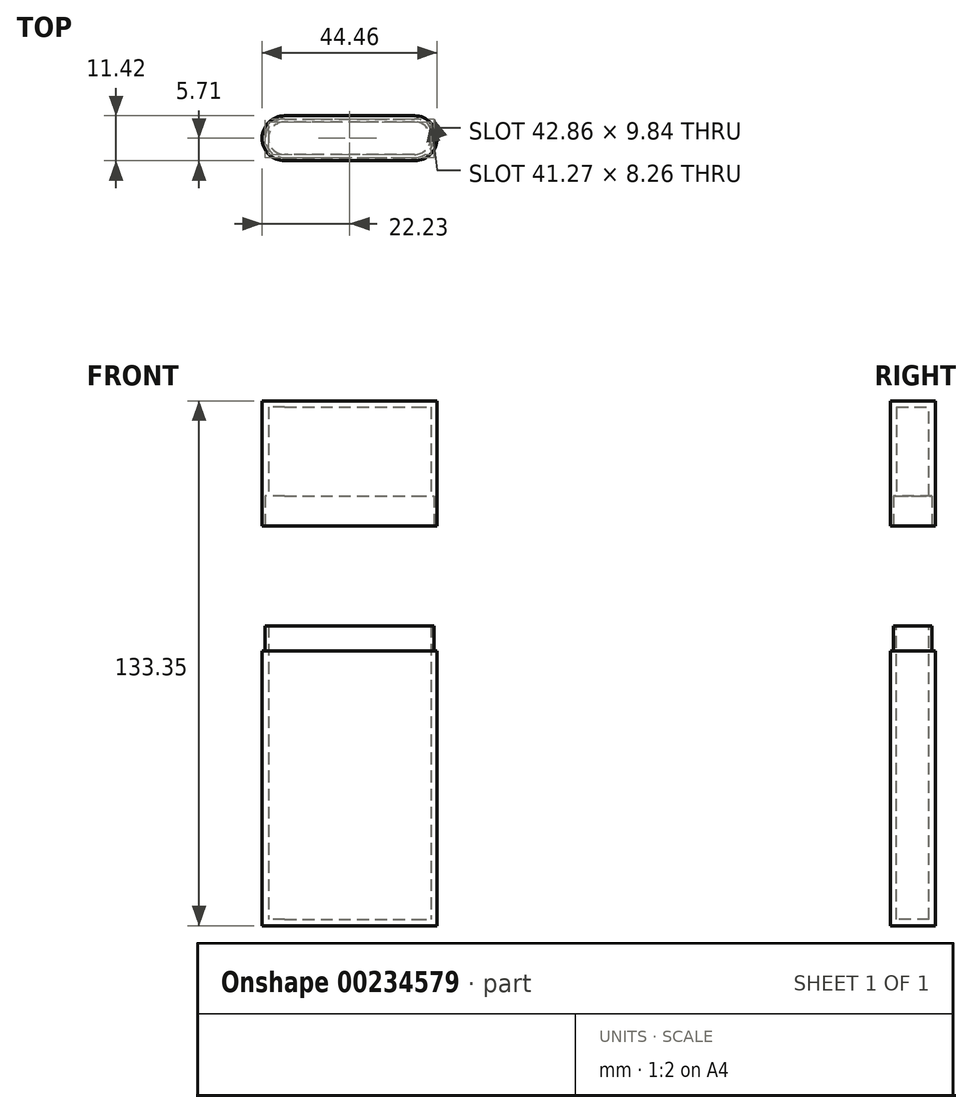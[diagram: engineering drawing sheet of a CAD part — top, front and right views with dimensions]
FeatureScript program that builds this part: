
annotation { "Feature Type Name" : "Feature", "Feature Type Description" : "" }
export const myFeature = defineFeature(function(context is Context, id is Id, definition is map)
    precondition{}
    {
        {
            var Q0;
            Q0=qCreatedBy(makeId("Top.planeOp"),FACE);
            var sketch = newSketch(context, id + "F0", { "sketchPlane" : qUnion([Q0])});
            skLineSegment(sketch, "E0.0", {"start": v(-16.51, 5.72) * mm, "end": v(16.51, 5.72) * mm});
            skArc(sketch, "E0.1", {"start": v(-16.51, 5.72) * mm, "mid": v(-22.23, 0) * mm, "end": v(-16.51, -5.72) * mm});
            skLineSegment(sketch, "E0.2", {"start": v(-16.51, -5.72) * mm, "end": v(16.51, -5.72) * mm});
            skArc(sketch, "E0.3", {"start": v(16.51, -5.72) * mm, "mid": v(22.23, 0) * mm, "end": v(16.51, 5.72) * mm});
            skPoint(sketch, "E1.start.orphan", {"position": v(-16.51, 4.13) * mm});
            skPoint(sketch, "E2.start.orphan", {"position": v(-16.51, -4.13) * mm});
            skSolve(sketch);
        }
        {
            assignVariable(context, id + "F1", {"mode" : VariableMode.ASSIGNED, "variableType" : VariableType.LENGTH, "measurementMode" : VariableMeasurementMode.DISTANCE, "name" : "Long", "lengthValue" : 76.2 * mm, "minmax" : VariableMinMaxSelection.MINIMUM, "extendEntities" : false, "measureFromAxis" : false, "distance" : 0 * mm, "xOffset" : 0 * mm, "yOffset" : 0 * mm, "zOffset" : 0 * mm, "componentSelector" : AxisWithCustom.DISTANCE, "customOffset" : 0 * mm, "radius" : false, "description" : ""});
        }
        {
            var Q0;
            Q0 = qSketchRegion(id + "F0", true);
            extrude(context, id + "F2", {"entities" : qUnion([Q0]), "flatOperationType" : FlatOperationType.REMOVE, "thickness1" : 6.35 * mm, "thickness2" : 0 * mm, "thickness" : 6.35 * mm, "offsetDistance" : 25.4 * mm, "startOffsetBound" : StartOffsetType.BLIND, "startOffsetDistance" : 25.4 * mm, "depth" : getVariable(context, 'Long'), "domain" : OperationDomain.MODEL});
        }
        {
            var Q0;
            Q0=makeQuery(id+"F2.opExtrude","CAP_FACE",FACE,{"disambiguationData":[OSD([sQuery(id+"F0.wireOp",EDGE,"E0.0"),sQuery(id+"F0.wireOp",EDGE,"E0.1"),sQuery(id+"F0.wireOp",EDGE,"E0.2"),sQuery(id+"F0.wireOp",EDGE,"E0.3")])],"isStart":false});
            shell(context, id + "F3", {"entities" : qUnion([Q0]), "thickness" : 1.59 * mm});
        }
        {
            var Q0;
            Q0=makeQuery(id+"F2.opExtrude","CAP_FACE",FACE,{"disambiguationData":[OSD([sQuery(id+"F0.wireOp",EDGE,"E0.0"),sQuery(id+"F0.wireOp",EDGE,"E0.1"),sQuery(id+"F0.wireOp",EDGE,"E0.2"),sQuery(id+"F0.wireOp",EDGE,"E0.3")])],"isStart":false});
            var sketch = newSketch(context, id + "F4", { "sketchPlane" : qUnion([Q0])});
            skArc(sketch, "E3.0", {"start": v(-16.51, 4.92) * mm, "mid": v(-21.43, 0) * mm, "end": v(-16.51, -4.92) * mm});
            skLineSegment(sketch, "E3.1", {"start": v(-16.51, 4.92) * mm, "end": v(16.51, 4.92) * mm});
            skArc(sketch, "E3.2", {"start": v(16.51, -4.92) * mm, "mid": v(21.43, 0) * mm, "end": v(16.51, 4.92) * mm});
            skLineSegment(sketch, "E3.3", {"start": v(-16.51, -4.92) * mm, "end": v(16.51, -4.92) * mm});
            skLineSegment(sketch, "E4", {"start": v(-16.51, 5.72) * mm, "end": v(16.51, 5.72) * mm});
            skLineSegment(sketch, "E5", {"start": v(-16.51, -5.72) * mm, "end": v(16.51, -5.72) * mm});
            skArc(sketch, "E6", {"start": v(16.51, -5.72) * mm, "mid": v(22.23, 0) * mm, "end": v(16.51, 5.72) * mm});
            skArc(sketch, "E7", {"start": v(-16.51, 5.72) * mm, "mid": v(-22.23, 0) * mm, "end": v(-16.51, -5.72) * mm});
            skSolve(sketch);
        }
        {
            var Q0;
            Q0 = qSketchRegion(id + "F4", true);
            extrude(context, id + "F5", {"entities" : qUnion([Q0]), "operationType" : NewBodyOperationType.REMOVE, "oppositeDirection" : true, "depth" : 6.35 * mm});
        }
        {
            var Q0;
            Q0=makeQuery(id+"F2.opExtrude","CAP_FACE",FACE,{"disambiguationData":[OSD([sQuery(id+"F0.wireOp",EDGE,"E0.0"),sQuery(id+"F0.wireOp",EDGE,"E0.1"),sQuery(id+"F0.wireOp",EDGE,"E0.2"),sQuery(id+"F0.wireOp",EDGE,"E0.3")])],"isStart":false});
            cPlane(context, id + "F6", {"entities" : qUnion([Q0]), "cplaneType" : CPlaneType.OFFSET, "offset" : 25.4 * mm, "width" : 152.4 * mm, "height" : 152.4 * mm});
        }
        {
            var Q0;
            Q0=qCreatedBy(id+"F6.planeOp",FACE);
            var sketch = newSketch(context, id + "F7", { "sketchPlane" : qUnion([Q0])});
            skLineSegment(sketch, "E8.0", {"start": v(-16.51, 5.72) * mm, "end": v(16.51, 5.72) * mm});
            skArc(sketch, "E8.1", {"start": v(-16.51, 5.72) * mm, "mid": v(-22.23, 0) * mm, "end": v(-16.51, -5.72) * mm});
            skLineSegment(sketch, "E8.2", {"start": v(-16.51, -5.72) * mm, "end": v(16.51, -5.72) * mm});
            skArc(sketch, "E8.3", {"start": v(16.51, -5.72) * mm, "mid": v(22.23, 0) * mm, "end": v(16.51, 5.72) * mm});
            skSolve(sketch);
        }
        {
            var Q0;
            Q0 = qSketchRegion(id + "F7", true);
            extrude(context, id + "F8", {"entities" : qUnion([Q0]), "depth" : 31.75 * mm});
        }
        {
            var Q0;
            Q0=makeQuery(id+"F8.opExtrude","CAP_FACE",FACE,{"disambiguationData":[OSD([sQuery(id+"F7.wireOp",EDGE,"E8.0"),sQuery(id+"F7.wireOp",EDGE,"E8.1"),sQuery(id+"F7.wireOp",EDGE,"E8.2"),sQuery(id+"F7.wireOp",EDGE,"E8.3")])],"isStart":true});
            shell(context, id + "F9", {"entities" : qUnion([Q0]), "thickness" : 1.59 * mm});
        }
        {
            var Q0;
            Q0=makeQuery(id+"F8.opExtrude","CAP_FACE",FACE,{"disambiguationData":[OSD([sQuery(id+"F7.wireOp",EDGE,"E8.0"),sQuery(id+"F7.wireOp",EDGE,"E8.1"),sQuery(id+"F7.wireOp",EDGE,"E8.2"),sQuery(id+"F7.wireOp",EDGE,"E8.3")])],"isStart":true});
            var sketch = newSketch(context, id + "F10", { "sketchPlane" : qUnion([Q0])});
            skLineSegment(sketch, "E9.0", {"start": v(-16.51, 4.92) * mm, "end": v(16.51, 4.92) * mm});
            skArc(sketch, "E9.1", {"start": v(-16.51, -4.92) * mm, "mid": v(-21.43, 0) * mm, "end": v(-16.51, 4.92) * mm});
            skLineSegment(sketch, "E9.2", {"start": v(-16.51, -4.92) * mm, "end": v(16.51, -4.92) * mm});
            skArc(sketch, "E9.3", {"start": v(16.51, 4.92) * mm, "mid": v(21.43, 0) * mm, "end": v(16.51, -4.92) * mm});
            skArc(sketch, "E10.0", {"start": v(-16.51, -4.13) * mm, "mid": v(-20.64, 0) * mm, "end": v(-16.51, 4.13) * mm});
            skLineSegment(sketch, "E10.1", {"start": v(-16.51, 4.13) * mm, "end": v(16.51, 4.13) * mm});
            skLineSegment(sketch, "E10.3", {"start": v(-16.51, -4.13) * mm, "end": v(16.5, -4.13) * mm});
            skSolve(sketch);
        }
        {
            var Q0;
            Q0 = qSketchRegion(id + "F10", true);
            extrude(context, id + "F11", {"entities" : qUnion([Q0]), "operationType" : NewBodyOperationType.REMOVE, "oppositeDirection" : true, "depth" : 7.62 * mm});
        }
    });
